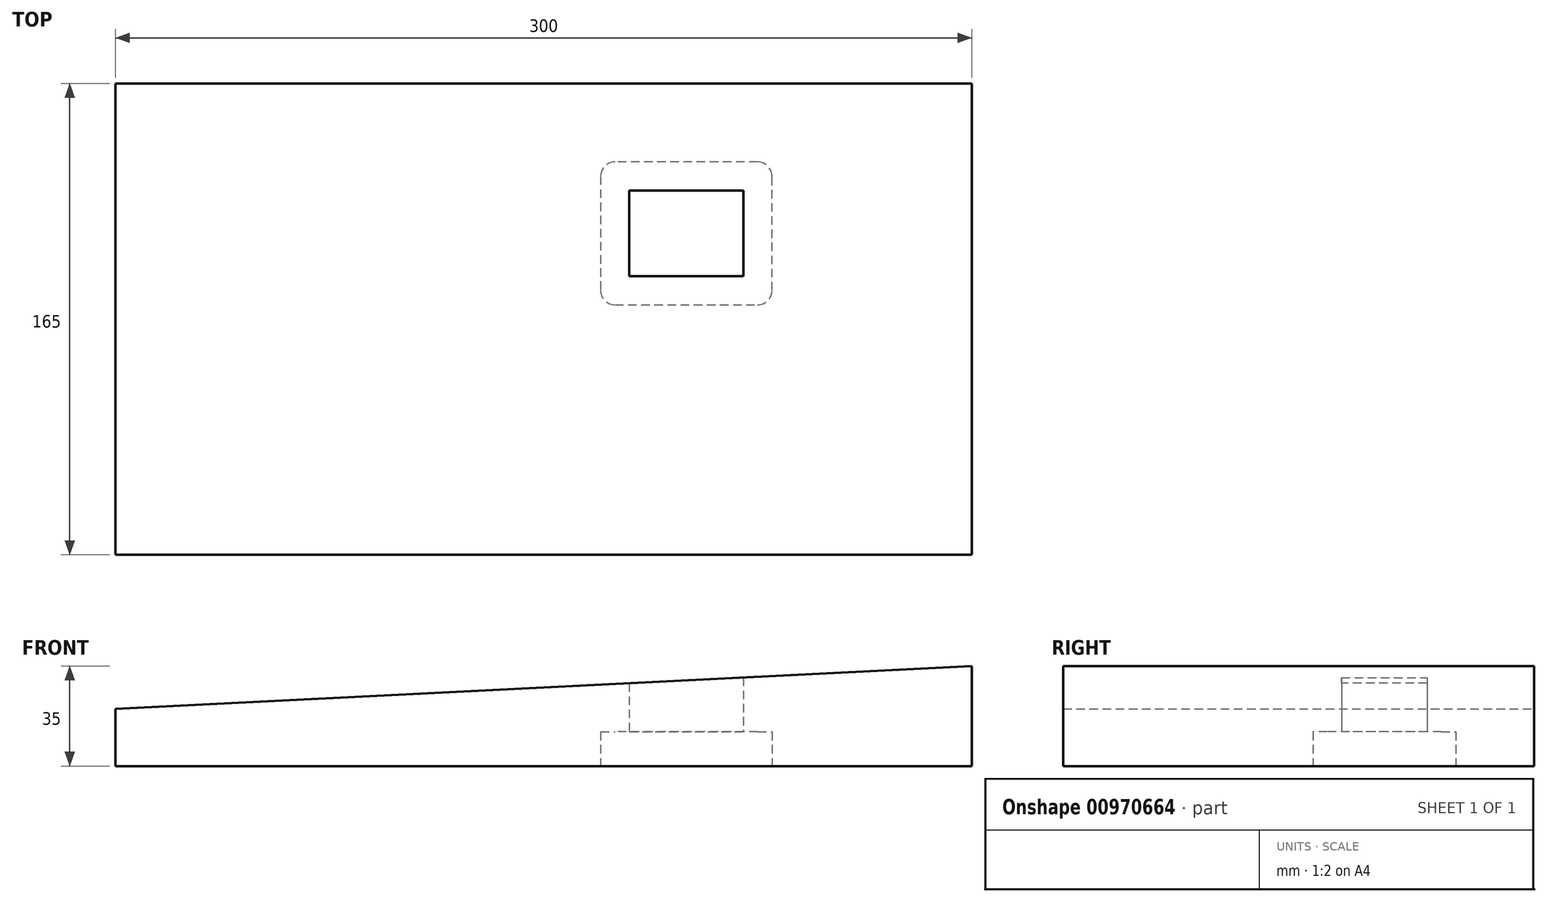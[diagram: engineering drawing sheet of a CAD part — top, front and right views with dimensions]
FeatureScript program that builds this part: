
annotation { "Feature Type Name" : "Feature", "Feature Type Description" : "" }
export const myFeature = defineFeature(function(context is Context, id is Id, definition is map)
    precondition{}
    {
        {
            var Q0;
            Q0=qCreatedBy(makeId("Front.planeOp"),FACE);
            var sketch = newSketch(context, id + "F0", { "sketchPlane" : qUnion([Q0])});
            skLineSegment(sketch, "E0", {"start": v(0, 31.52) * mm, "end": v(300, 31.52) * mm});
            skLineSegment(sketch, "E1", {"start": v(300, 31.52) * mm, "end": v(300, 66.52) * mm});
            skLineSegment(sketch, "E2", {"start": v(300, 66.52) * mm, "end": v(0, 51.52) * mm});
            skLineSegment(sketch, "E3", {"start": v(0, 51.52) * mm, "end": v(0, 31.52) * mm});
            skSolve(sketch);
        }
        {
            var Q0;
            Q0=makeQuery(id+"F0.imprint","IMPRINT",FACE,{"disambiguationData":[TD([[makeQuery(id+"F0.imprint","IMPRINT",EDGE,{"derivedFrom":sQuery(id+"F0.wireOp",EDGE,"E0")}),1.0]])]});
            extrude(context, id + "F1", {"entities" : qUnion([Q0]), "depth" : 165 * mm, "offsetDistance" : 25 * mm});
        }
        {
            var Q0;
            Q0=makeQuery(id+"F1.opExtrude","SWEPT_FACE",FACE,{"disambiguationData":[OSD([sQuery(id+"F0.wireOp",EDGE,"E0")])]});
            var sketch = newSketch(context, id + "F2", { "sketchPlane" : qUnion([Q0])});
            skLineSegment(sketch, "E4", {"start": v(180, 67.5) * mm, "end": v(220, 67.5) * mm});
            skLineSegment(sketch, "E5", {"start": v(220, 67.5) * mm, "end": v(220, 37.5) * mm});
            skLineSegment(sketch, "E6", {"start": v(220, 37.5) * mm, "end": v(180, 37.5) * mm});
            skLineSegment(sketch, "E7", {"start": v(180, 37.5) * mm, "end": v(180, 67.5) * mm});
            skSolve(sketch);
        }
        {
            var Q0;
            Q0=makeQuery(id+"F2.imprint","IMPRINT",FACE,{"disambiguationData":[TD([[makeQuery(id+"F2.imprint","IMPRINT",EDGE,{"derivedFrom":sQuery(id+"F2.wireOp",EDGE,"E4")}),-1.0]])]});
            extrude(context, id + "F3", {"entities" : qUnion([Q0]), "operationType" : NewBodyOperationType.REMOVE, "endBound" : BoundingType.THROUGH_ALL, "oppositeDirection" : true, "depth" : 25 * mm, "offsetDistance" : 25 * mm});
        }
        {
            var Q0;
            Q0=makeQuery(id+"F1.opExtrude","SWEPT_FACE",FACE,{"disambiguationData":[OSD([sQuery(id+"F0.wireOp",EDGE,"E0")])]});
            var sketch = newSketch(context, id + "F4", { "sketchPlane" : qUnion([Q0])});
            skLineSegment(sketch, "E8", {"start": v(170, 32.5) * mm, "end": v(170, 72.5) * mm});
            skLineSegment(sketch, "E9", {"start": v(175, 77.5) * mm, "end": v(225, 77.5) * mm});
            skLineSegment(sketch, "E10", {"start": v(230, 72.5) * mm, "end": v(230, 32.5) * mm});
            skLineSegment(sketch, "E11", {"start": v(225, 27.5) * mm, "end": v(175, 27.5) * mm});
            skPoint(sketch, "E12.visualSharp", {"position": v(70, 30) * mm});
            skArc(sketch, "E12.filletArc", {"start": v(170, 32.5) * mm, "mid": v(171.46, 28.96) * mm, "end": v(175, 27.5) * mm});
            skPoint(sketch, "E13.visualSharp", {"position": v(170, 77.5) * mm});
            skArc(sketch, "E13.filletArc", {"start": v(175, 77.5) * mm, "mid": v(171.46, 76.04) * mm, "end": v(170, 72.5) * mm});
            skPoint(sketch, "E14.visualSharp", {"position": v(230, 27.5) * mm});
            skArc(sketch, "E14.filletArc", {"start": v(225, 27.5) * mm, "mid": v(228.54, 28.96) * mm, "end": v(230, 32.5) * mm});
            skPoint(sketch, "E15.visualSharp", {"position": v(230, 77.5) * mm});
            skArc(sketch, "E15.filletArc", {"start": v(230, 72.5) * mm, "mid": v(228.54, 76.04) * mm, "end": v(225, 77.5) * mm});
            skSolve(sketch);
        }
        {
            var Q0;
            Q0=makeQuery(id+"F4.imprint","IMPRINT",FACE,{"disambiguationData":[TD([[makeQuery(id+"F4.imprint","IMPRINT",EDGE,{"derivedFrom":sQuery(id+"F4.wireOp",EDGE,"E8")}),-1.0]])]});
            extrude(context, id + "F5", {"entities" : qUnion([Q0]), "operationType" : NewBodyOperationType.REMOVE, "oppositeDirection" : true, "depth" : 12 * mm, "offsetDistance" : 25 * mm});
        }
    });
